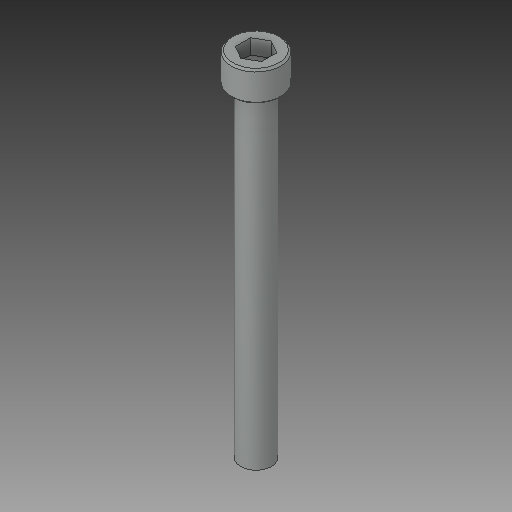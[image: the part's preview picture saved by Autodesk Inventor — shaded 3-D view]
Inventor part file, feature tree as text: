
AUTODESK INVENTOR PART (.ipt)
format: ipt  version: 2017 (Build 210142000, 142)  size: 93,184 bytes
history: native  units: in
note: dims shown in document units (in); Inventor stores cm internally (conversion verified against a paired STEP export)
features: chamfer x1
ambient origin geometry x8: Origin, YZ Plane, XZ Plane, XY Plane, X Axis, Y Axis, Z Axis, Center Point
bodies: Solid1 (feature_tree)
feature tree (1):
  chamfer  "Chamfer2"  [1 undecoded]
note: 1 required parameter value undecoded (feature->parameter linkage not recoverable at this tier; creation-order binding heuristic only, values carry confidence <= 0.55)
